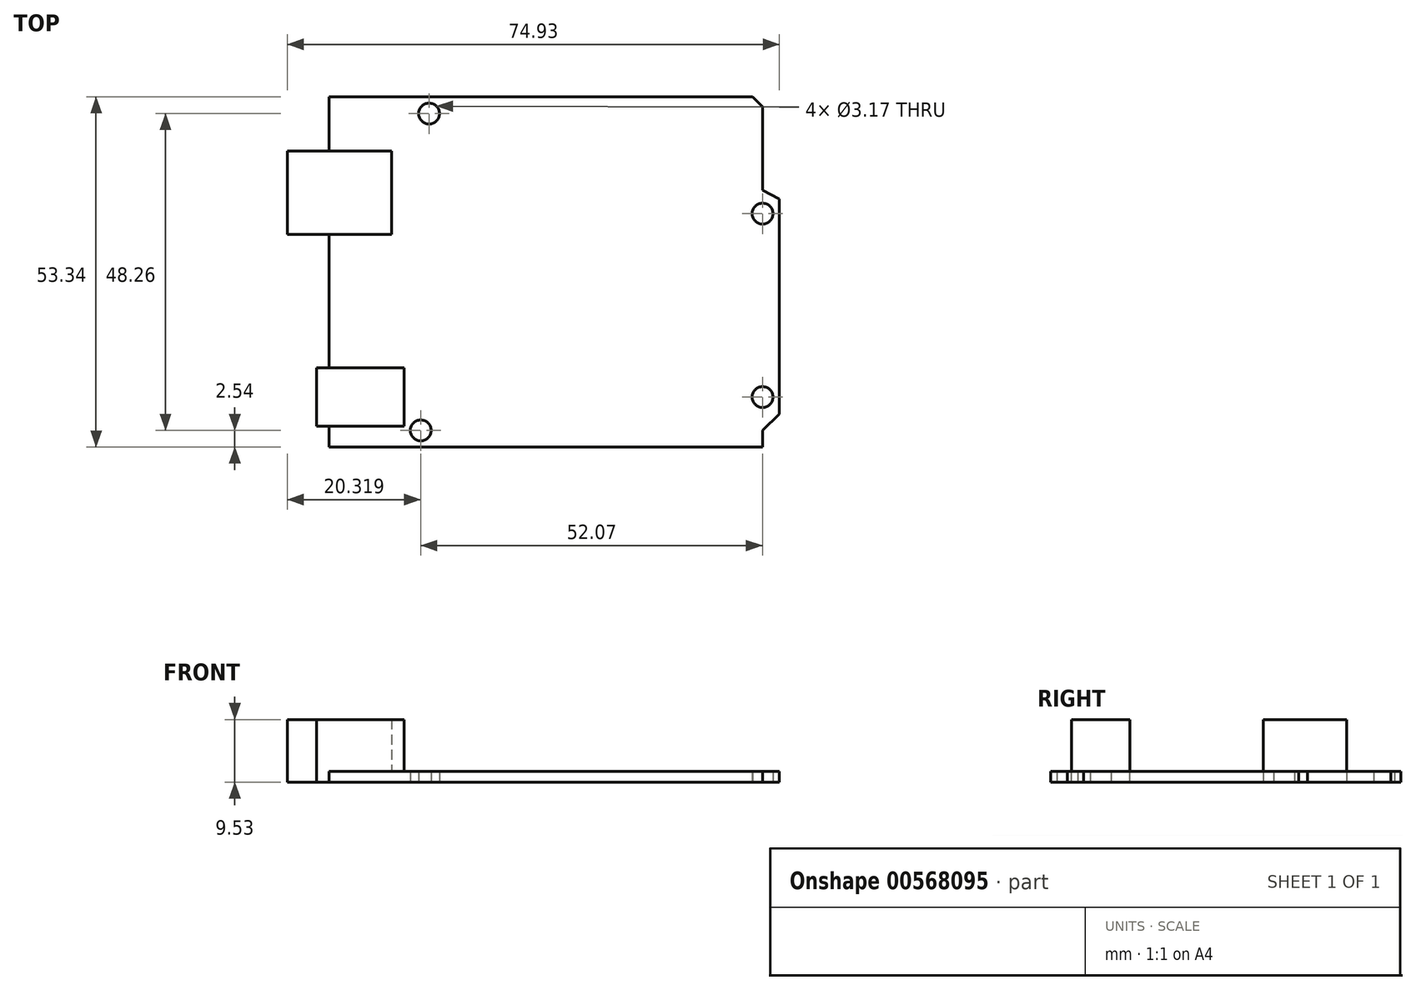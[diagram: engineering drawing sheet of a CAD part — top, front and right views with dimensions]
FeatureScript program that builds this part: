
annotation { "Feature Type Name" : "Feature", "Feature Type Description" : "" }
export const myFeature = defineFeature(function(context is Context, id is Id, definition is map)
    precondition{}
    {
        {
            var Q0;
            Q0=qCreatedBy(makeId("Top.planeOp"),FACE);
            var sketch = newSketch(context, id + "F0", { "sketchPlane" : qUnion([Q0])});
            skLineSegment(sketch, "E0", {"start": v(-33.71, 0) * mm, "end": v(32.33, 0) * mm});
            skLineSegment(sketch, "E1", {"start": v(32.33, 0) * mm, "end": v(32.33, 2.54) * mm});
            skPoint(sketch, "E2", {"position": v(139.55, -75.82) * mm});
            skPoint(sketch, "E3", {"position": v(224.93, -61.76) * mm});
            skPoint(sketch, "E4", {"position": v(222.92, 16.59) * mm});
            skPoint(sketch, "E5", {"position": v(219.91, 51.24) * mm});
            skPoint(sketch, "E6", {"position": v(203.34, 62.8) * mm});
            skLineSegment(sketch, "E7", {"start": v(-33.71, 0) * mm, "end": v(-33.71, 53.34) * mm});
            skLineSegment(sketch, "E8", {"start": v(-33.71, 53.34) * mm, "end": v(30.8, 53.34) * mm});
            skLineSegment(sketch, "E9", {"start": v(32.33, 2.54) * mm, "end": v(34.87, 5.02) * mm});
            skLineSegment(sketch, "E10", {"start": v(34.87, 5.02) * mm, "end": v(34.87, 37.78) * mm});
            skCircle(sketch, "E11", {"center": v(-18.47, 50.8) * mm, "radius": 1.59 * mm});
            skCircle(sketch, "E12", {"center": v(-19.74, 2.54) * mm, "radius": 1.59 * mm});
            skCircle(sketch, "E13", {"center": v(32.33, 35.56) * mm, "radius": 1.59 * mm});
            skCircle(sketch, "E14", {"center": v(32.33, 7.62) * mm, "radius": 1.59 * mm});
            skPoint(sketch, "E15", {"position": v(32.33, 51.82) * mm});
            skLineSegment(sketch, "E16", {"start": v(30.8, 53.34) * mm, "end": v(32.33, 51.82) * mm});
            skLineSegment(sketch, "E17", {"start": v(32.33, 51.82) * mm, "end": v(32.33, 39.12) * mm});
            skLineSegment(sketch, "E18", {"start": v(32.33, 39.12) * mm, "end": v(34.87, 37.78) * mm});
            skSolve(sketch);
        }
        {
            var Q0;
            Q0=qCreatedBy(makeId("Top.planeOp"),FACE);
            var sketch = newSketch(context, id + "F1", { "sketchPlane" : qUnion([Q0])});
            skLineSegment(sketch, "E19", {"start": v(-22.28, 0) * mm, "end": v(-22.28, 3.18) * mm});
            skLineSegment(sketch, "E20.bottom", {"start": v(-22.28, 3.18) * mm, "end": v(-35.62, 3.18) * mm});
            skLineSegment(sketch, "E20.top", {"start": v(-22.28, 12.06) * mm, "end": v(-35.62, 12.06) * mm});
            skLineSegment(sketch, "E20.left", {"start": v(-22.28, 3.18) * mm, "end": v(-22.28, 12.07) * mm});
            skLineSegment(sketch, "E20.right", {"start": v(-35.62, 3.17) * mm, "end": v(-35.62, 12.06) * mm});
            skLineSegment(sketch, "E21.bottom", {"start": v(-40.06, 45.09) * mm, "end": v(-24.19, 45.09) * mm});
            skLineSegment(sketch, "E21.top", {"start": v(-40.06, 32.39) * mm, "end": v(-24.19, 32.39) * mm});
            skLineSegment(sketch, "E21.left", {"start": v(-40.06, 45.09) * mm, "end": v(-40.06, 32.39) * mm});
            skLineSegment(sketch, "E21.right", {"start": v(-24.19, 45.09) * mm, "end": v(-24.19, 32.39) * mm});
            skSolve(sketch);
        }
        {
            var Q0;
            Q0 = qSketchRegion(id + "F0", true);
            extrude(context, id + "F2", {"entities" : qUnion([Q0]), "depth" : 1.65 * mm, "offsetDistance" : 25.4 * mm});
        }
        {
            var Q0;
            Q0 = qSketchRegion(id + "F1", true);
            extrude(context, id + "F3", {"entities" : qUnion([Q0]), "operationType" : NewBodyOperationType.ADD, "depth" : 9.52 * mm, "offsetDistance" : 25.4 * mm});
        }
    });
